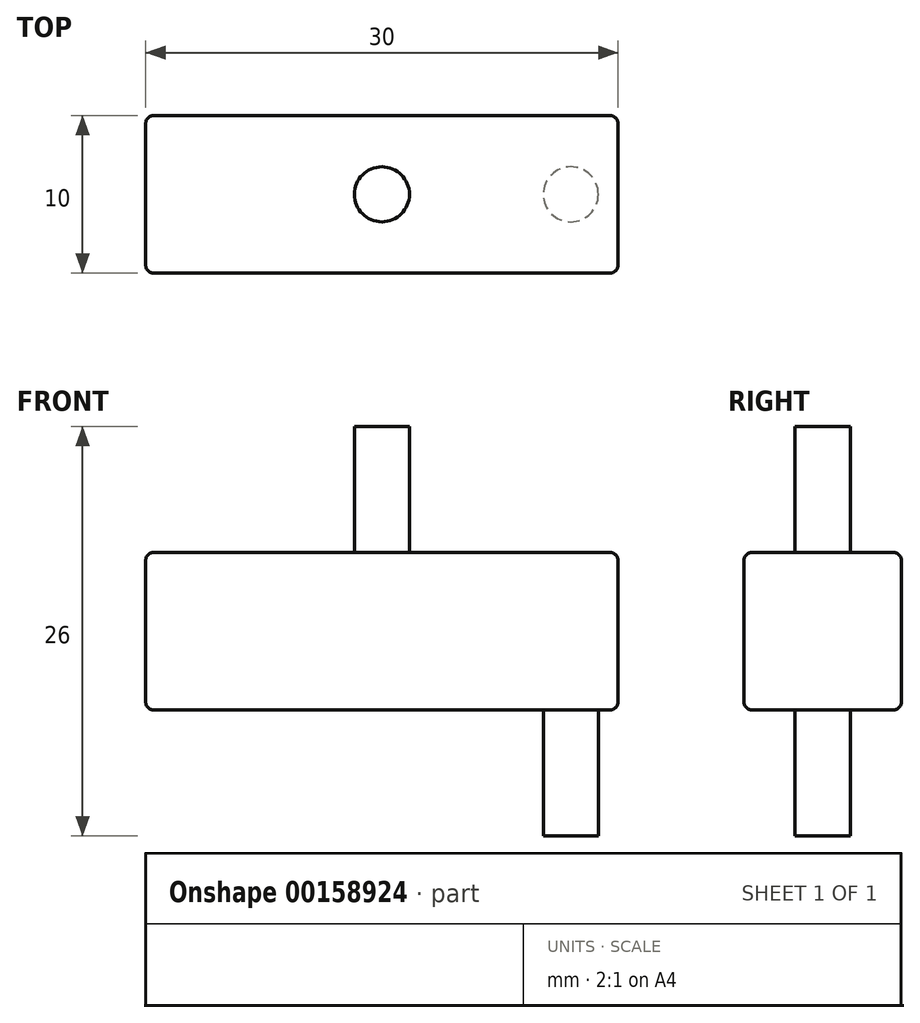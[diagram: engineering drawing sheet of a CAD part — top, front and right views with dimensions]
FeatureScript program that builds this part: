
annotation { "Feature Type Name" : "Feature", "Feature Type Description" : "" }
export const myFeature = defineFeature(function(context is Context, id is Id, definition is map)
    precondition{}
    {
        {
            var Q0;
            Q0=qCreatedBy(makeId("Front.planeOp"),FACE);
            var sketch = newSketch(context, id + "F0", { "sketchPlane" : qUnion([Q0])});
            skLineSegment(sketch, "E0.bottom", {"start": v(-15, 5) * mm, "end": v(15, 5) * mm});
            skLineSegment(sketch, "E0.top", {"start": v(-15, -5) * mm, "end": v(15, -5) * mm});
            skLineSegment(sketch, "E0.left", {"start": v(-15, 5) * mm, "end": v(-15, -5) * mm});
            skLineSegment(sketch, "E0.right", {"start": v(15, 5) * mm, "end": v(15, -5) * mm});
            skPoint(sketch, "E0.middle", {"position": v(0, 0) * mm});
            skSolve(sketch);
        }
        {
            var Q0;
            Q0=makeQuery(id+"F0.imprint","IMPRINT",FACE,{"disambiguationData":[TD([[makeQuery(id+"F0.imprint","IMPRINT",EDGE,{"derivedFrom":sQuery(id+"F0.wireOp",EDGE,"E0.bottom")}),-1.0]])]});
            extrude(context, id + "F1", {"entities" : qUnion([Q0]), "oppositeDirection" : true, "depth" : 10 * mm});
        }
        {
            var Q0;
            Q0=makeQuery(id+"F1.opExtrude","SWEPT_FACE",FACE,{"disambiguationData":[OSD([sQuery(id+"F0.wireOp",EDGE,"E0.bottom")])]});
            var sketch = newSketch(context, id + "F2", { "sketchPlane" : qUnion([Q0])});
            skCircle(sketch, "E1", {"center": v(0, 5) * mm, "radius": 1.75 * mm});
            skPoint(sketch, "E1.centerSnap0", {"position": v(-15, 5) * mm});
            skSolve(sketch);
        }
        {
            var Q0;
            Q0 = qSketchRegion(id + "F2", true);
            extrude(context, id + "F3", {"entities" : qUnion([Q0]), "operationType" : NewBodyOperationType.ADD, "depth" : 8 * mm});
        }
        {
            var Q0;
            Q0=makeQuery(id+"F1.opExtrude","SWEPT_FACE",FACE,{"disambiguationData":[OSD([sQuery(id+"F0.wireOp",EDGE,"E0.top")])]});
            var sketch = newSketch(context, id + "F4", { "sketchPlane" : qUnion([Q0])});
            skCircle(sketch, "E2", {"center": v(12, -5) * mm, "radius": 1.75 * mm});
            skPoint(sketch, "E2.centerSnap0", {"position": v(15, -5) * mm});
            skSolve(sketch);
        }
        {
            var Q0;
            Q0 = qSketchRegion(id + "F4", true);
            extrude(context, id + "F5", {"entities" : qUnion([Q0]), "operationType" : NewBodyOperationType.ADD, "depth" : 8 * mm});
        }
        {
            var Q0;
            Q0=makeQuery(id+"F1.opExtrude","CAP_EDGE",EDGE,{"disambiguationData":[OSD([sQuery(id+"F0.wireOp",EDGE,"E0.bottom")])],"isStart":true});
            fillet(context, id + "F6", {"entities" : qUnion([Q0]), "radius" : 0.5 * mm, "tangentPropagation" : true, "allowEdgeOverflow" : false});
        }
        {
            var Q0;
            Q0=makeQuery(id+"F1.opExtrude","SWEPT_EDGE",EDGE,{"disambiguationData":[OSD([sQuery(id+"F0.wireOp",EDGE,"E0.bottom"),sQuery(id+"F0.wireOp",EDGE,"E0.right")])]});
            var Q1;
            Q1=makeQuery(id+"F1.opExtrude","SWEPT_EDGE",EDGE,{"disambiguationData":[OSD([sQuery(id+"F0.wireOp",EDGE,"E0.bottom"),sQuery(id+"F0.wireOp",EDGE,"E0.left")])]});
            var Q2;
            Q2=makeQuery(id+"F1.opExtrude","CAP_EDGE",EDGE,{"disambiguationData":[OSD([sQuery(id+"F0.wireOp",EDGE,"E0.bottom")])],"isStart":false});
            var Q3;
            Q3=makeQuery(id+"F1.opExtrude","SWEPT_EDGE",EDGE,{"disambiguationData":[OSD([sQuery(id+"F0.wireOp",EDGE,"E0.top"),sQuery(id+"F0.wireOp",EDGE,"E0.right")])]});
            var Q4;
            Q4=makeQuery(id+"F1.opExtrude","CAP_EDGE",EDGE,{"disambiguationData":[OSD([sQuery(id+"F0.wireOp",EDGE,"E0.right")])],"isStart":false});
            fillet(context, id + "F7", {"entities" : qUnion([Q0, Q1, Q2, Q3, Q4]), "radius" : 0.5 * mm, "tangentPropagation" : true, "allowEdgeOverflow" : false});
        }
        {
            var Q0;
            Q0=makeQuery(id+"F1.opExtrude","CAP_EDGE",EDGE,{"disambiguationData":[OSD([sQuery(id+"F0.wireOp",EDGE,"E0.top")])],"isStart":false});
            var Q1;
            Q1=makeQuery(id+"F1.opExtrude","CAP_EDGE",EDGE,{"disambiguationData":[OSD([sQuery(id+"F0.wireOp",EDGE,"E0.top")])],"isStart":true});
            var Q2;
            Q2=makeQuery(id+"F1.opExtrude","CAP_EDGE",EDGE,{"disambiguationData":[OSD([sQuery(id+"F0.wireOp",EDGE,"E0.left")])],"isStart":false});
            fillet(context, id + "F8", {"entities" : qUnion([Q0, Q1, Q2]), "radius" : 0.5 * mm, "tangentPropagation" : true, "allowEdgeOverflow" : false});
        }
    });
